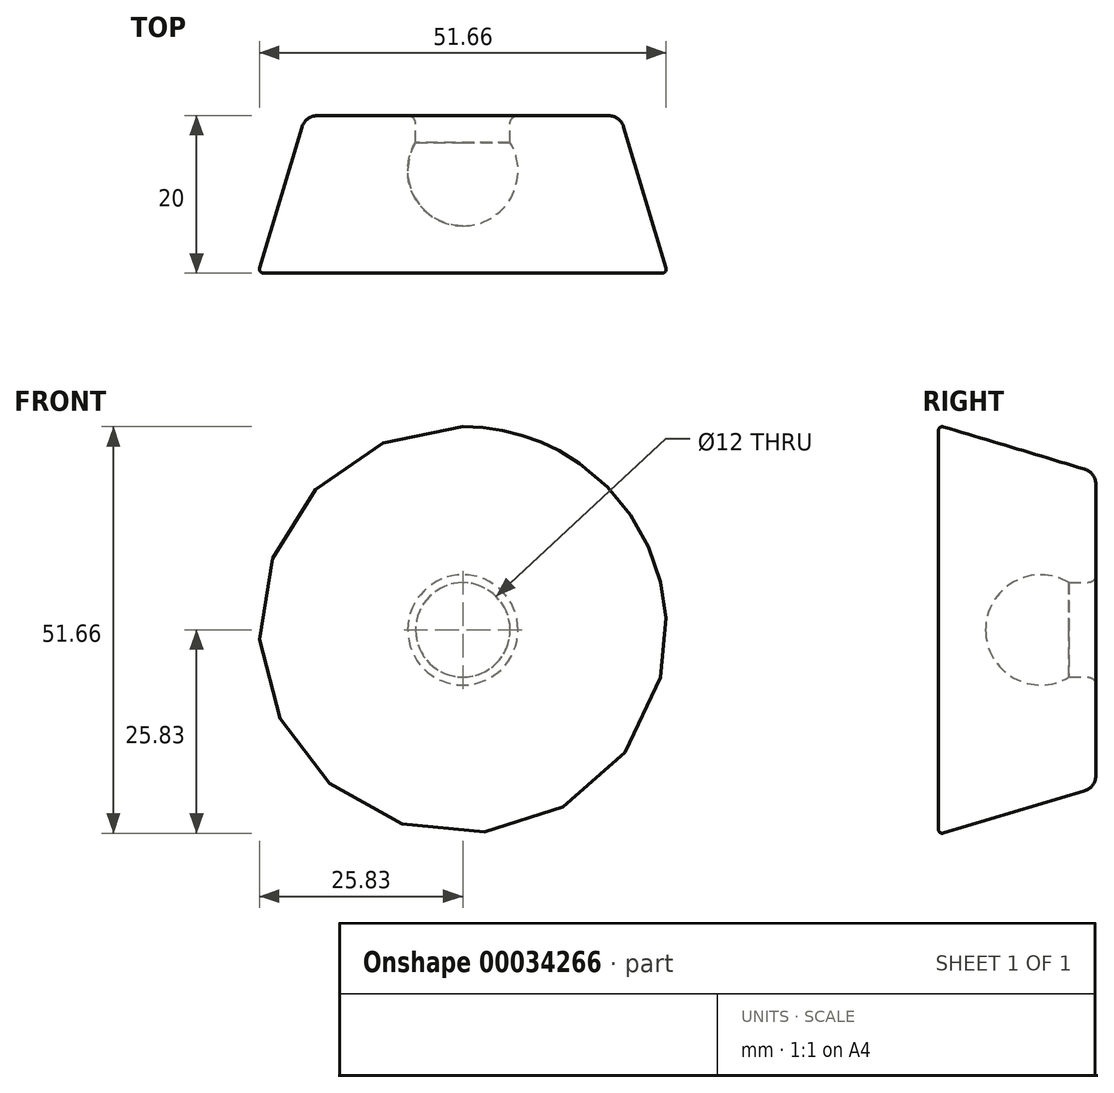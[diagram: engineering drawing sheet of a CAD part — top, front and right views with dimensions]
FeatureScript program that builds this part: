
annotation { "Feature Type Name" : "Feature", "Feature Type Description" : "" }
export const myFeature = defineFeature(function(context is Context, id is Id, definition is map)
    precondition{}
    {
        {
            var Q0;
            Q0=qCreatedBy(makeId("Top.planeOp"),FACE);
            var sketch = newSketch(context, id + "F0", { "sketchPlane" : qUnion([Q0])});
            skLineSegment(sketch, "E0", {"start": v(-25.8, 0.64) * mm, "end": v(-20.43, 18.57) * mm});
            skLineSegment(sketch, "E1", {"start": v(-18.51, 20) * mm, "end": v(-7, 20) * mm});
            skLineSegment(sketch, "E2", {"start": v(-6, 19) * mm, "end": v(-6, 16.6) * mm});
            skLineSegment(sketch, "E3", {"start": v(-6, 0) * mm, "end": v(-25.33, 0) * mm});
            skArc(sketch, "E4", {"start": v(-6, 16.6) * mm, "mid": v(-6.1, 9.55) * mm, "end": v(0, 6) * mm});
            skLineSegment(sketch, "E5", {"start": v(0, 0) * mm, "end": v(-6, 0) * mm});
            skLineSegment(sketch, "E6", {"start": v(0, 6) * mm, "end": v(0, 0) * mm});
            skPoint(sketch, "E7.visualSharp", {"position": v(-26, 0) * mm});
            skArc(sketch, "E7.filletArc", {"start": v(-25.8, 0.64) * mm, "mid": v(-25.73, 0.2) * mm, "end": v(-25.33, 0) * mm});
            skPoint(sketch, "E8.visualSharp", {"position": v(-20, 20) * mm});
            skArc(sketch, "E8.filletArc", {"start": v(-18.51, 20) * mm, "mid": v(-19.7, 19.6) * mm, "end": v(-20.43, 18.57) * mm});
            skPoint(sketch, "E9.visualSharp", {"position": v(-6, 20) * mm});
            skArc(sketch, "E9.filletArc", {"start": v(-6, 19) * mm, "mid": v(-6.3, 19.7) * mm, "end": v(-7, 20) * mm});
            skSolve(sketch);
        }
        {
            var Q0;
            Q0=makeQuery(id+"F0.imprint","IMPRINT",FACE,{"disambiguationData":[TD([[makeQuery(id+"F0.imprint","IMPRINT",EDGE,{"derivedFrom":sQuery(id+"F0.wireOp",EDGE,"E0")}),-1.0]])]});
            var Q1;
            Q1=sQuery(id+"F0.wireOp",EDGE,"E6");
            revolve(context, id + "F1", {"entities" : qUnion([Q0]), "axis" : qUnion([Q1]), "revolveType" : RevolveType.FULL});
        }
    });
